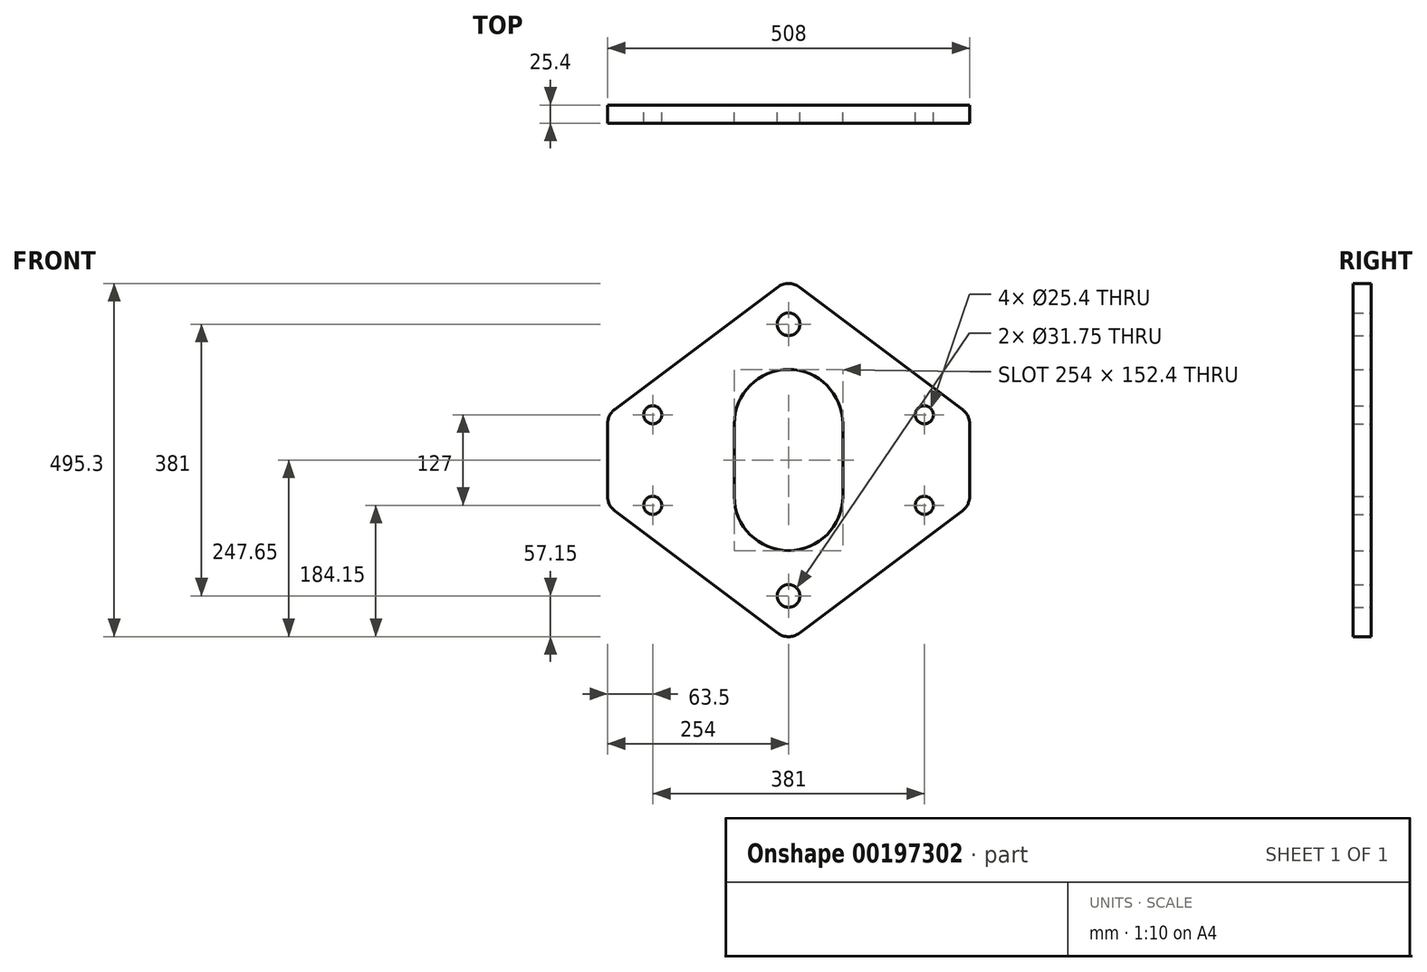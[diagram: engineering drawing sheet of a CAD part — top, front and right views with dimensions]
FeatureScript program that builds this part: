
annotation { "Feature Type Name" : "Feature", "Feature Type Description" : "" }
export const myFeature = defineFeature(function(context is Context, id is Id, definition is map)
    precondition{}
    {
        {
            var Q0;
            Q0=qCreatedBy(makeId("Front.planeOp"),FACE);
            var sketch = newSketch(context, id + "F0", { "sketchPlane" : qUnion([Q0])});
            skLineSegment(sketch, "E0.left", {"start": v(254, 50.8) * mm, "end": v(254, -50.8) * mm});
            skLineSegment(sketch, "E0.right", {"start": v(-254, 50.8) * mm, "end": v(-254, -50.8) * mm});
            skPoint(sketch, "E0.middle", {"position": v(0, 0) * mm});
            skLineSegment(sketch, "E1", {"start": v(-15.24, 242.57) * mm, "end": v(-243.84, 71.12) * mm});
            skLineSegment(sketch, "E2.MirrorCS", {"start": v(15.24, 242.57) * mm, "end": v(243.84, 71.12) * mm});
            skLineSegment(sketch, "E3.MirrorCS", {"start": v(15.24, -242.57) * mm, "end": v(243.84, -71.12) * mm});
            skLineSegment(sketch, "E4.MirrorCS", {"start": v(-15.24, -242.57) * mm, "end": v(-243.84, -71.12) * mm});
            skCircle(sketch, "E5", {"center": v(0, 190.5) * mm, "radius": 15.88 * mm});
            skCircle(sketch, "E6.MirrorC", {"center": v(0, -190.5) * mm, "radius": 15.88 * mm});
            skCircle(sketch, "E7", {"center": v(-190.5, 63.5) * mm, "radius": 12.7 * mm});
            skCircle(sketch, "E8.0.1.0", {"center": v(-190.5, -63.5) * mm, "radius": 12.7 * mm});
            skCircle(sketch, "E8.1.0.0", {"center": v(190.5, 63.5) * mm, "radius": 12.7 * mm});
            skCircle(sketch, "E8.1.1.0", {"center": v(190.5, -63.5) * mm, "radius": 12.7 * mm});
            skLineSegment(sketch, "E8.direction1", {"start": v(-190.5, 63.5) * mm, "end": v(190.5, 63.5) * mm, "construction": true});
            skLineSegment(sketch, "E8.direction2", {"start": v(-190.5, 63.5) * mm, "end": v(-190.5, -63.5) * mm, "construction": true});
            skPoint(sketch, "E9.visualSharp", {"position": v(0, 254) * mm});
            skArc(sketch, "E9.filletArc", {"start": v(15.24, 242.57) * mm, "mid": v(0, 247.65) * mm, "end": v(-15.24, 242.57) * mm});
            skPoint(sketch, "E10.visualSharp", {"position": v(254, 63.5) * mm});
            skArc(sketch, "E10.filletArc", {"start": v(254, 50.8) * mm, "mid": v(251.32, 62.16) * mm, "end": v(243.84, 71.12) * mm});
            skPoint(sketch, "E11.visualSharp", {"position": v(254, -63.5) * mm});
            skArc(sketch, "E11.filletArc", {"start": v(243.84, -71.12) * mm, "mid": v(251.32, -62.16) * mm, "end": v(254, -50.8) * mm});
            skPoint(sketch, "E12.visualSharp", {"position": v(0, -254) * mm});
            skArc(sketch, "E12.filletArc", {"start": v(-15.24, -242.57) * mm, "mid": v(0, -247.65) * mm, "end": v(15.24, -242.57) * mm});
            skPoint(sketch, "E13.visualSharp", {"position": v(-254, -63.5) * mm});
            skArc(sketch, "E13.filletArc", {"start": v(-254, -50.8) * mm, "mid": v(-251.32, -62.16) * mm, "end": v(-243.84, -71.12) * mm});
            skPoint(sketch, "E14.visualSharp", {"position": v(-254, 63.5) * mm});
            skArc(sketch, "E14.filletArc", {"start": v(-243.84, 71.12) * mm, "mid": v(-251.32, 62.16) * mm, "end": v(-254, 50.8) * mm});
            skArc(sketch, "E15", {"start": v(76.2, 50.8) * mm, "mid": v(0, 127) * mm, "end": v(-76.2, 50.8) * mm});
            skArc(sketch, "E16.MirrorC", {"start": v(76.2, -50.8) * mm, "mid": v(0, -127) * mm, "end": v(-76.2, -50.8) * mm});
            skLineSegment(sketch, "E17", {"start": v(76.2, 50.8) * mm, "end": v(76.2, -50.8) * mm});
            skLineSegment(sketch, "E18.MirrorCS", {"start": v(-76.2, 50.8) * mm, "end": v(-76.2, -50.8) * mm});
            skSolve(sketch);
        }
        {
            var Q0;
            Q0=makeQuery(id+"F0.imprint","IMPRINT",FACE,{"disambiguationData":[TD([[makeQuery(id+"F0.imprint","IMPRINT",EDGE,{"derivedFrom":sQuery(id+"F0.wireOp",EDGE,"E0.left")}),-1.0]])]});
            extrude(context, id + "F1", {"entities" : qUnion([Q0]), "endBound" : BoundingType.SYMMETRIC, "depth" : 25.4 * mm});
        }
    });
